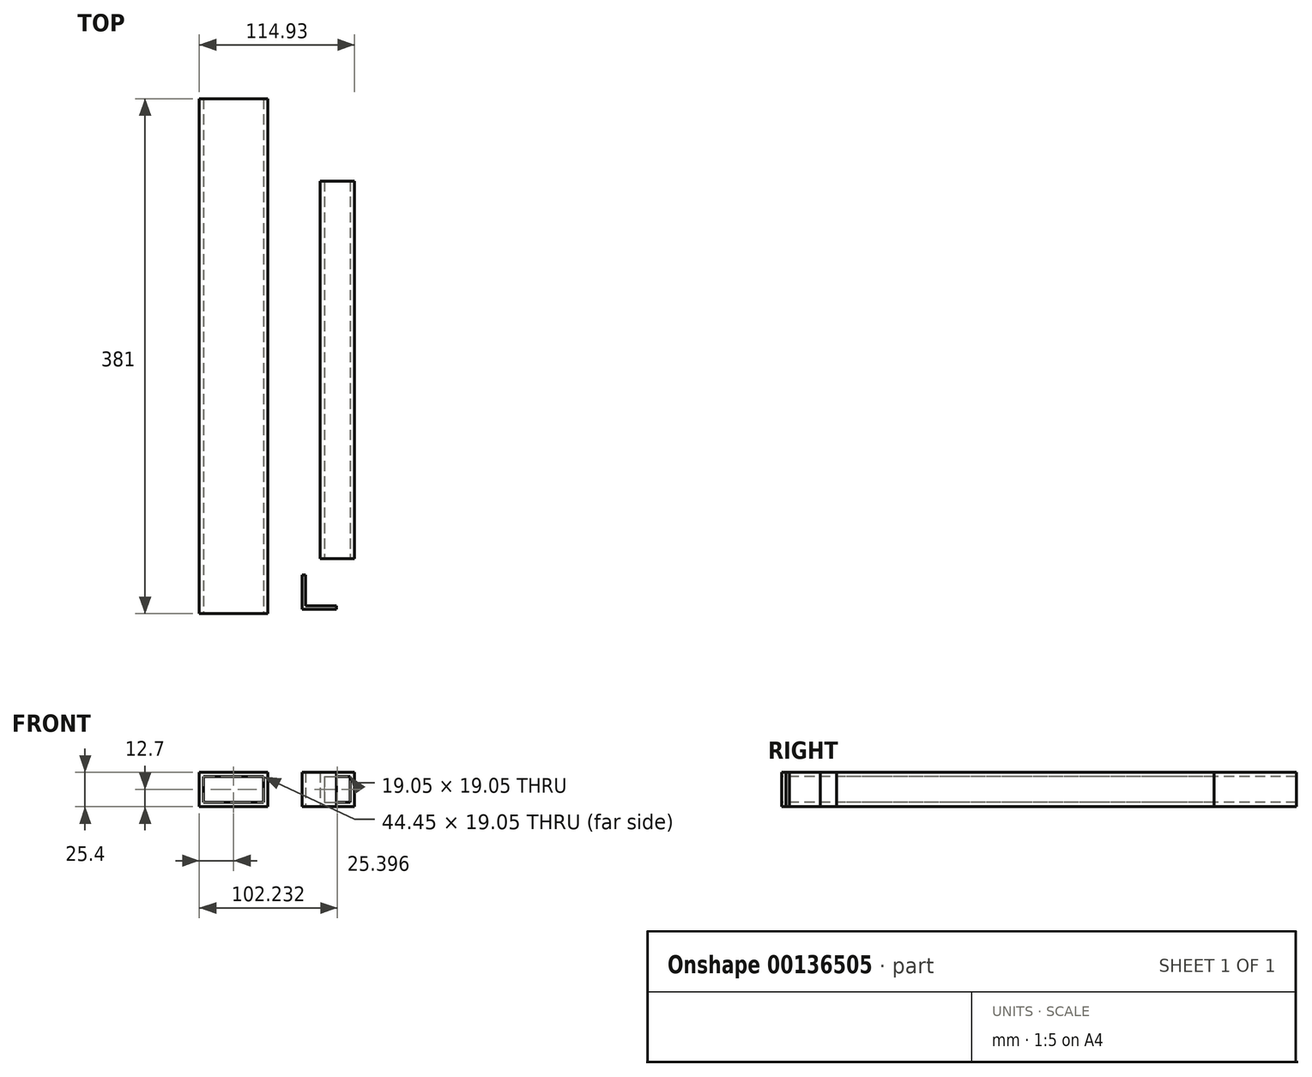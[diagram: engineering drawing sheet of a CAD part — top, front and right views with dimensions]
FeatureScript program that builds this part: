
annotation { "Feature Type Name" : "Feature", "Feature Type Description" : "" }
export const myFeature = defineFeature(function(context is Context, id is Id, definition is map)
    precondition{}
    {
        {
            var Q0;
            Q0=qCreatedBy(makeId("Top.planeOp"),FACE);
            var sketch = newSketch(context, id + "F0", { "sketchPlane" : qUnion([Q0])});
            skLineSegment(sketch, "E0.bottom", {"start": v(-56.28, 312.16) * mm, "end": v(-5.48, 312.16) * mm});
            skLineSegment(sketch, "E0.top", {"start": v(-56.28, -68.84) * mm, "end": v(-5.48, -68.84) * mm});
            skLineSegment(sketch, "E0.left", {"start": v(-56.28, 312.16) * mm, "end": v(-56.28, -68.84) * mm});
            skLineSegment(sketch, "E0.right", {"start": v(-5.48, 312.16) * mm, "end": v(-5.48, -68.84) * mm});
            skSolve(sketch);
        }
        {
            var Q0;
            Q0=makeQuery(id+"F0.imprint","IMPRINT",FACE,{"disambiguationData":[TD([[makeQuery(id+"F0.imprint","IMPRINT",EDGE,{"derivedFrom":sQuery(id+"F0.wireOp",EDGE,"E0.bottom")}),-1.0]])]});
            extrude(context, id + "F1", {"entities" : qUnion([Q0]), "depth" : 25.4 * mm});
        }
        {
            var Q0;
            Q0=makeQuery(id+"F1.opExtrude","SWEPT_FACE",FACE,{"disambiguationData":[OSD([sQuery(id+"F0.wireOp",EDGE,"E0.top")])]});
            var Q1;
            Q1=makeQuery(id+"F1.opExtrude","SWEPT_FACE",FACE,{"disambiguationData":[OSD([sQuery(id+"F0.wireOp",EDGE,"E0.bottom")])]});
            shell(context, id + "F2", {"entities" : qUnion([Q0, Q1]), "thickness" : 3.17 * mm});
        }
        {
            var Q0;
            Q0=qCreatedBy(makeId("Top.planeOp"),FACE);
            var sketch = newSketch(context, id + "F3", { "sketchPlane" : qUnion([Q0])});
            skLineSegment(sketch, "E1.bottom", {"start": v(33.25, 251.2) * mm, "end": v(58.65, 251.2) * mm});
            skLineSegment(sketch, "E1.top", {"start": v(33.25, -28.2) * mm, "end": v(58.65, -28.2) * mm});
            skLineSegment(sketch, "E1.left", {"start": v(33.25, 251.2) * mm, "end": v(33.25, -28.2) * mm});
            skLineSegment(sketch, "E1.right", {"start": v(58.65, 251.2) * mm, "end": v(58.65, -28.2) * mm});
            skSolve(sketch);
        }
        {
            var Q0;
            Q0=makeQuery(id+"F3.imprint","IMPRINT",FACE,{"disambiguationData":[TD([[makeQuery(id+"F3.imprint","IMPRINT",EDGE,{"derivedFrom":sQuery(id+"F3.wireOp",EDGE,"E1.bottom")}),-1.0]])]});
            extrude(context, id + "F4", {"entities" : qUnion([Q0]), "depth" : 25.4 * mm});
        }
        {
            var Q0;
            Q0=makeQuery(id+"F4.opExtrude","SWEPT_FACE",FACE,{"disambiguationData":[OSD([sQuery(id+"F3.wireOp",EDGE,"E1.top")])]});
            var Q1;
            Q1=makeQuery(id+"F4.opExtrude","SWEPT_FACE",FACE,{"disambiguationData":[OSD([sQuery(id+"F3.wireOp",EDGE,"E1.bottom")])]});
            shell(context, id + "F5", {"entities" : qUnion([Q0, Q1]), "thickness" : 3.17 * mm});
        }
        {
            var Q0;
            Q0=qCreatedBy(makeId("Top.planeOp"),FACE);
            var sketch = newSketch(context, id + "F6", { "sketchPlane" : qUnion([Q0])});
            skLineSegment(sketch, "E2", {"start": v(19.9, -40.14) * mm, "end": v(19.9, -65.54) * mm});
            skLineSegment(sketch, "E3", {"start": v(19.9, -65.54) * mm, "end": v(45.3, -65.54) * mm});
            skLineSegment(sketch, "E4", {"start": v(45.3, -65.54) * mm, "end": v(45.3, -63) * mm});
            skLineSegment(sketch, "E5", {"start": v(45.3, -63) * mm, "end": v(22.44, -63) * mm});
            skLineSegment(sketch, "E6", {"start": v(22.44, -63) * mm, "end": v(22.44, -40.14) * mm});
            skLineSegment(sketch, "E7", {"start": v(22.44, -40.14) * mm, "end": v(19.9, -40.14) * mm});
            skSolve(sketch);
        }
        {
            var Q0;
            Q0 = qSketchRegion(id + "F6", true);
            extrude(context, id + "F7", {"entities" : qUnion([Q0]), "depth" : 25.4 * mm});
        }
    });
